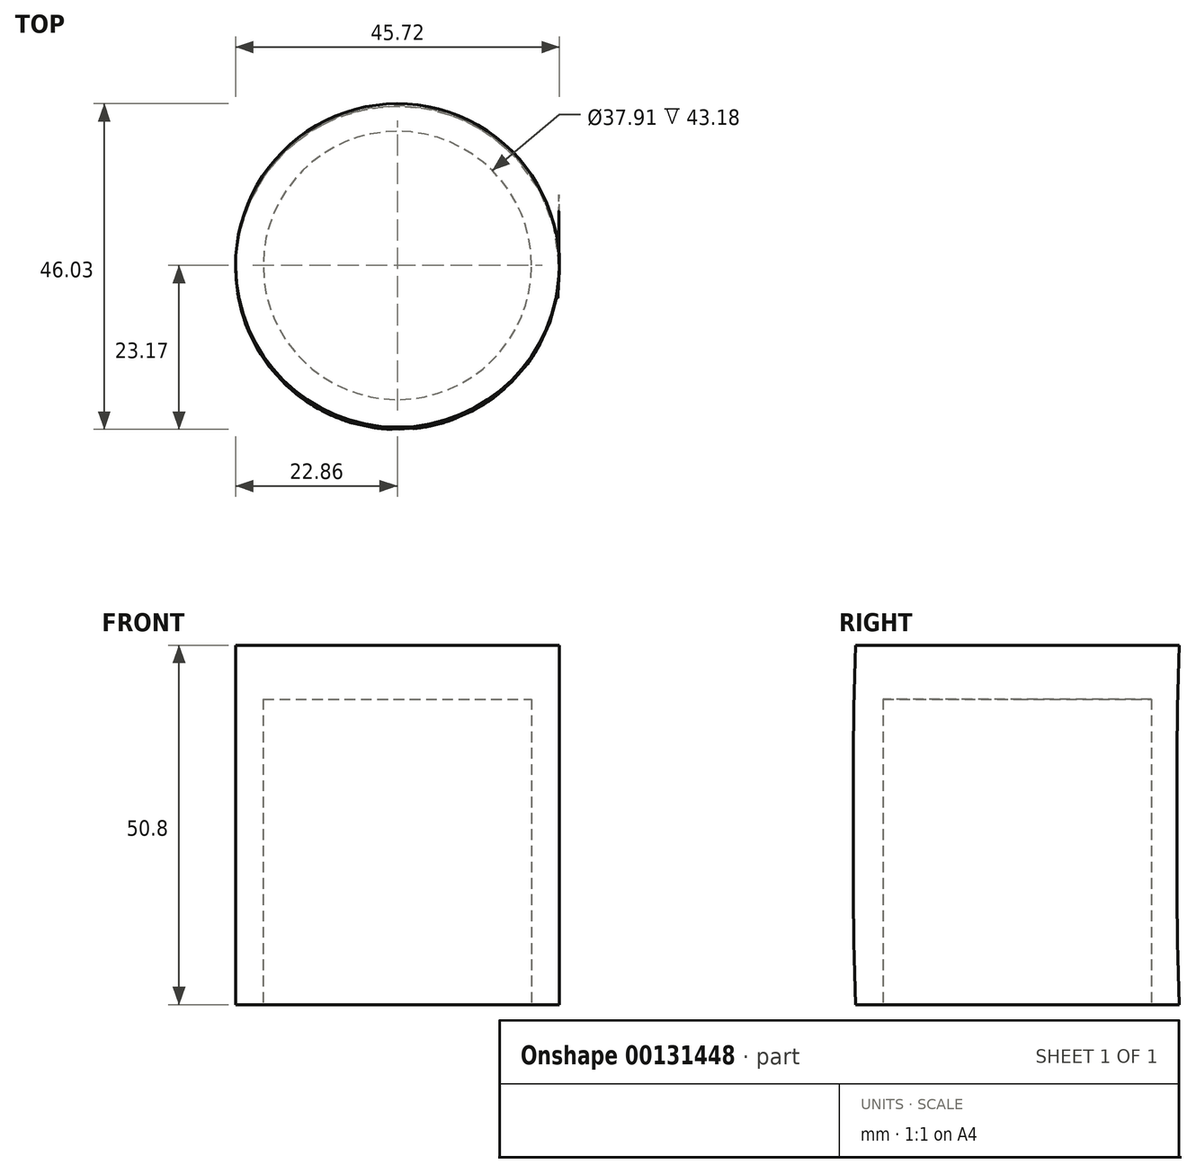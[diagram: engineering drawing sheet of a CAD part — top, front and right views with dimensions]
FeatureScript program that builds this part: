
annotation { "Feature Type Name" : "Feature", "Feature Type Description" : "" }
export const myFeature = defineFeature(function(context is Context, id is Id, definition is map)
    precondition{}
    {
        {
            var Q0;
            Q0=qCreatedBy(makeId("Top.planeOp"),FACE);
            var sketch = newSketch(context, id + "F0", { "sketchPlane" : qUnion([Q0])});
            skCircle(sketch, "E0", {"center": v(0, 0) * mm, "radius": 22.86 * mm});
            skSolve(sketch);
        }
        {
            var Q0;
            Q0=qCreatedBy(makeId("Top.planeOp"),FACE);
            cPlane(context, id + "F1", {"entities" : qUnion([Q0]), "cplaneType" : CPlaneType.OFFSET, "offset" : 12.7 * mm, "oppositeDirection" : true, "width" : 152.4 * mm, "height" : 152.4 * mm});
        }
        {
            var Q0;
            Q0=qCreatedBy(id+"F1.planeOp",FACE);
            var sketch = newSketch(context, id + "F2", { "sketchPlane" : qUnion([Q0])});
            skCircle(sketch, "E1", {"center": v(0, -0.3) * mm, "radius": 22.86 * mm});
            skSolve(sketch);
        }
        {
            var Q0;
            Q0=qCreatedBy(id+"F1.planeOp",FACE);
            cPlane(context, id + "F3", {"entities" : qUnion([Q0]), "cplaneType" : CPlaneType.OFFSET, "offset" : 12.7 * mm, "oppositeDirection" : true, "width" : 152.4 * mm, "height" : 152.4 * mm});
        }
        {
            var Q0;
            Q0=qCreatedBy(id+"F3.planeOp",FACE);
            var sketch = newSketch(context, id + "F4", { "sketchPlane" : qUnion([Q0])});
            skCircle(sketch, "E2", {"center": v(0, -0.3) * mm, "radius": 22.86 * mm});
            skSolve(sketch);
        }
        {
            var Q0;
            Q0=qCreatedBy(id+"F3.planeOp",FACE);
            cPlane(context, id + "F5", {"entities" : qUnion([Q0]), "cplaneType" : CPlaneType.OFFSET, "offset" : 12.7 * mm, "oppositeDirection" : true, "width" : 152.4 * mm, "height" : 152.4 * mm});
        }
        {
            var Q0;
            Q0=qCreatedBy(id+"F5.planeOp",FACE);
            var sketch = newSketch(context, id + "F6", { "sketchPlane" : qUnion([Q0])});
            skCircle(sketch, "E3", {"center": v(0, -0.3) * mm, "radius": 22.86 * mm});
            skSolve(sketch);
        }
        {
            var Q0;
            Q0=qCreatedBy(id+"F5.planeOp",FACE);
            cPlane(context, id + "F7", {"entities" : qUnion([Q0]), "cplaneType" : CPlaneType.OFFSET, "offset" : 12.7 * mm, "oppositeDirection" : true, "width" : 152.4 * mm, "height" : 152.4 * mm});
        }
        {
            var Q0;
            Q0=qCreatedBy(id+"F7.planeOp",FACE);
            var sketch = newSketch(context, id + "F8", { "sketchPlane" : qUnion([Q0])});
            skCircle(sketch, "E4", {"center": v(0, 0) * mm, "radius": 22.86 * mm});
            skSolve(sketch);
        }
        {
            var Q0;
            Q0 = qSketchRegion(id + "F0", true);
            var Q1;
            Q1 = qSketchRegion(id + "F2", true);
            var Q2;
            Q2 = qSketchRegion(id + "F4", true);
            var Q3;
            Q3 = qSketchRegion(id + "F6", true);
            var Q4;
            Q4 = qSketchRegion(id + "F8", true);
            loft(context, id + "F9", {"sheetProfilesArray" : [{ "sheetProfileEntities" : qUnion([Q0]) }, { "sheetProfileEntities" : qUnion([Q1]) }, { "sheetProfileEntities" : qUnion([Q2]) }, { "sheetProfileEntities" : qUnion([Q3]) }, { "sheetProfileEntities" : qUnion([Q4]) }]});
        }
        {
            var Q0;
            Q0=makeQuery(id+"F9.opLoft","CAP_FACE",FACE,{"disambiguationData":[OSD([makeQuery(id+"F8.imprint","IMPRINT",FACE,{"disambiguationData":[TD([[makeQuery(id+"F8.imprint","IMPRINT",EDGE,{"derivedFrom":sQuery(id+"F8.wireOp",EDGE,"E4")}),1.0]])]})])],"isStart":true});
            var sketch = newSketch(context, id + "F10", { "sketchPlane" : qUnion([Q0])});
            skCircle(sketch, "E5", {"center": v(0, 0) * mm, "radius": 18.95 * mm});
            skSolve(sketch);
        }
        {
            var Q0;
            Q0 = qSketchRegion(id + "F10", true);
            extrude(context, id + "F11", {"entities" : qUnion([Q0]), "operationType" : NewBodyOperationType.REMOVE, "oppositeDirection" : true, "depth" : 43.18 * mm});
        }
    });
